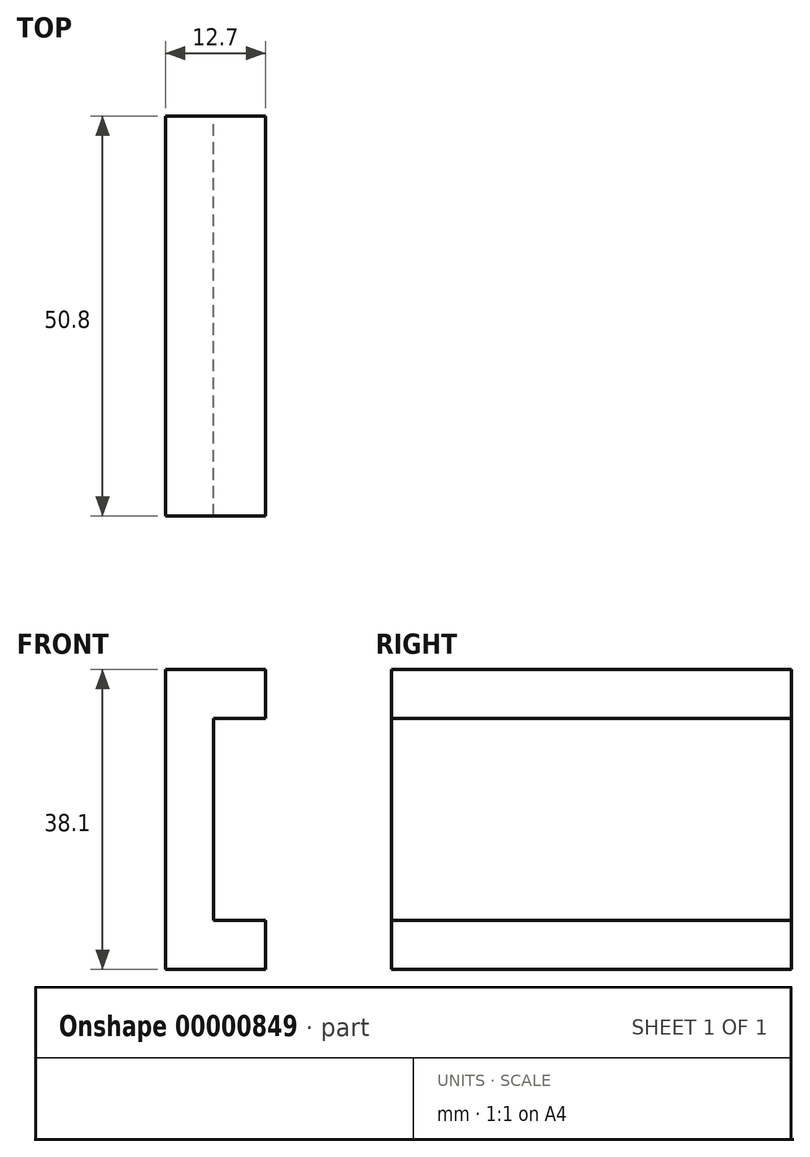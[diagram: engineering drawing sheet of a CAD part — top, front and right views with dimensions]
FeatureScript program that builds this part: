
annotation { "Feature Type Name" : "Feature", "Feature Type Description" : "" }
export const myFeature = defineFeature(function(context is Context, id is Id, definition is map)
    precondition{}
    {
        {
            var Q0;
            Q0=qCreatedBy(makeId("Front.planeOp"),FACE);
            var sketch = newSketch(context, id + "F0", { "sketchPlane" : qUnion([Q0])});
            skLineSegment(sketch, "E0.bottom", {"start": v(-12.7, 31.88) * mm, "end": v(0, 31.88) * mm});
            skLineSegment(sketch, "E0.top", {"start": v(-12.7, -6.22) * mm, "end": v(0, -6.22) * mm});
            skLineSegment(sketch, "E0.left", {"start": v(-12.7, 31.88) * mm, "end": v(-12.7, -6.22) * mm});
            skLineSegment(sketch, "E1", {"start": v(0, 25.65) * mm, "end": v(-6.6, 25.65) * mm});
            skLineSegment(sketch, "E2", {"start": v(-6.6, 25.65) * mm, "end": v(-6.6, 0) * mm});
            skLineSegment(sketch, "E3", {"start": v(-6.6, 0) * mm, "end": v(0, 0) * mm});
            skLineSegment(sketch, "E4", {"start": v(0, 31.88) * mm, "end": v(0, 25.65) * mm});
            skLineSegment(sketch, "E5", {"start": v(0, -6.22) * mm, "end": v(0, 0) * mm});
            skLineSegment(sketch, "E6", {"start": v(0, 0) * mm, "end": v(0, 40.1) * mm, "construction": true});
            skSolve(sketch);
        }
        {
            var Q0;
            Q0 = qSketchRegion(id + "F0", true);
            extrude(context, id + "F1", {"entities" : qUnion([Q0]), "depth" : 50.8 * mm});
        }
    });
